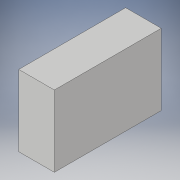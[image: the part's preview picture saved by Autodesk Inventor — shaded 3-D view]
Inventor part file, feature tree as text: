
AUTODESK INVENTOR PART (.ipt)
format: ipt  version: 2017 (Build 210142000, 142)  size: 100,864 bytes
history: native  units: in
note: dims shown in document units (in); Inventor stores cm internally (conversion verified against a paired STEP export)
features: sketch x2, extrude x1, hole x1
ambient origin geometry x8: Origin, YZ Plane, XZ Plane, XY Plane, X Axis, Y Axis, Z Axis, Center Point
bodies: Solid1 (feature_tree)
feature tree (4):
  extrude  "Extrusion1"  Depth=0.5in
  hole  "Hole1"  [1 undecoded]
  sketch  "Sketch1"  dims[d0=0.25in d1=0.5in]
  sketch  "Sketch2"  dims[d2=0.75in d3=0.0in d4=0.125in d5=0.125in d6=0.13in d7=0.155in d8=0.375in d9=0.25in d10=0.5635in d11=0.2in d12=0.8108in]
note: 1 required parameter value undecoded (feature->parameter linkage not recoverable at this tier; creation-order binding heuristic only, values carry confidence <= 0.55)
